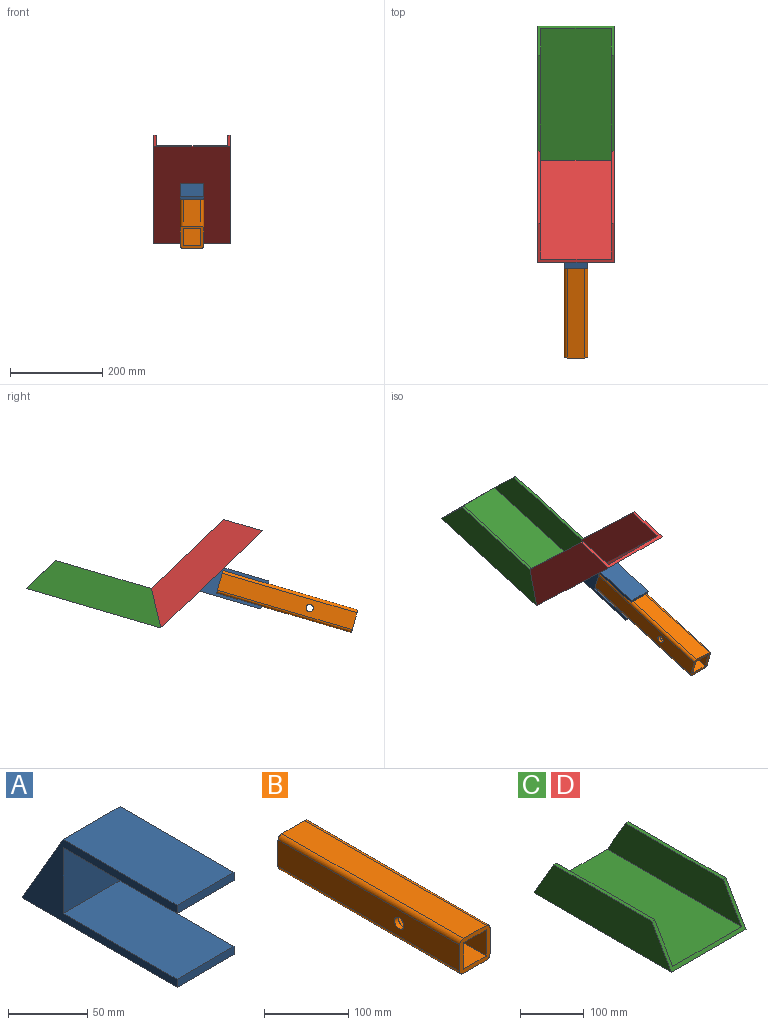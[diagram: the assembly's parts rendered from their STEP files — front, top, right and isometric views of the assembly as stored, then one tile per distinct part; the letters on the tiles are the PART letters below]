
ASSEMBLY  parts=4 mates=3
PART A: 10 faces, bbox 50.8x138.3x63.5 mm
  f0: plane 50.8x50.8mm, normal (0,-1,0), area 2580.6mm2, adj f1,f7,f8,f9
  f1: plane 101.6x50.8mm, normal (0,0,1), area 5161.3mm2, adj f0,f2,f8,f9
  f2: plane 50.8x6.35mm, normal (0,-1,0), area 322.6mm2, adj f1,f3,f8,f9
  f3: plane 138.26x50.8mm, normal (0,0,-1), area 7023.7mm2, adj f2,f4,f8,f9
  f4: plane 63.5x50.8mm, normal (0,0.87,0.5), area 3724.8mm2, adj f3,f5,f8,f9
  f5: plane 101.6x50.8mm, normal (0,0,1), area 5161.3mm2, adj f4,f6,f8,f9
  f6: plane 50.8x6.35mm, normal (0,-1,0), area 322.6mm2, adj f5,f7,f8,f9
  f7: plane 101.6x50.8mm, normal (0,0,-1), area 5161.3mm2, adj f0,f6,f8,f9
  f8: plane 138.26x63.5mm, normal (1,0,0), area 2454.3mm2, adj f0,f1,f2,f3,f4,f5,f6,f7
  f9: plane 138.26x63.5mm, normal (-1,0,0), area 2454.3mm2, adj f0,f1,f2,f3,f4,f5,f6,f7
PART B: 16 faces, bbox 50.8x304.8x50.8 mm
  f0: plane 304.8x38.1mm, normal (1,0,0), area 11414.9mm2, adj f1,f7,f8,f9,f14
  f1: cylinder r=6.35mm len=304.8mm, axis (0,1,0), area 3040.2mm2, adj f0,f2,f8,f9
  f2: plane 304.8x38.1mm, normal (0,0,1), area 11612.9mm2, adj f1,f3,f8,f9
  f3: cylinder r=6.35mm len=304.8mm, axis (0,1,0), area 3040.2mm2, adj f2,f4,f8,f9
  f4: plane 304.8x38.1mm, normal (-1,0,0), area 11414.9mm2, adj f3,f5,f8,f9,f15
  f5: cylinder r=6.35mm len=304.8mm, axis (0,1,0), area 3040.2mm2, adj f4,f6,f8,f9
  f6: plane 304.8x38.1mm, normal (0,0,-1), area 11612.9mm2, adj f5,f7,f8,f9
  f7: cylinder r=6.35mm len=304.8mm, axis (0,1,0), area 3040.2mm2, adj f0,f6,f8,f9
  f8: plane 50.8x50.8mm, normal (0,-1,0), area 1094.4mm2, adj f0,f1,f2,f3,f4,f5,f6,f7
  f9: plane 50.8x50.8mm, normal (0,1,0), area 1094.4mm2, adj f0,f1,f2,f3,f4,f5,f6,f7
  f10: plane 304.8x38.1mm, normal (1,0,0), area 11414.9mm2, adj f8,f9,f11,f13,f15
  f11: plane 304.8x38.1mm, normal (0,0,1), area 11612.9mm2, adj f8,f9,f10,f12
  f12: plane 304.8x38.1mm, normal (-1,0,0), area 11414.9mm2, adj f8,f9,f11,f13,f14
  f13: plane 304.8x38.1mm, normal (0,0,-1), area 11612.9mm2, adj f8,f9,f10,f12
  f14: cylinder r=7.94mm len=15.88mm, axis (1,0,0), area 316.7mm2, adj f0,f12
  f15: cylinder r=7.94mm len=15.88mm, axis (1,0,0), area 316.7mm2, adj f4,f10
PART C: 10 faces, bbox 165.1x304.8x76.2 mm
  f0: plane 216.81x6.35mm, normal (0,0,1), area 1376.8mm2, adj f3,f6,f7,f9
  f1: plane 304.8x76.2mm, normal (-1,0,0), area 19873.4mm2, adj f5,f6,f8,f9
  f2: plane 297.47x152.4mm, normal (0,0,1), area 45334.1mm2, adj f3,f4,f6,f9
  f3: plane 297.47x69.85mm, normal (-1,0,0), area 17961.2mm2, adj f0,f2,f6,f9
  f4: plane 297.47x69.85mm, normal (1,0,0), area 17961.2mm2, adj f2,f6,f8,f9
  f5: plane 304.8x165.1mm, normal (0,0,-1), area 50322.5mm2, adj f1,f6,f7,f9
  f6: plane 165.1x76.2mm, normal (0,0.87,0.5), area 2234.9mm2, adj f0,f1,f2,f3,f4,f5,f7,f8
  f7: plane 304.8x76.2mm, normal (1,0,0), area 19873.4mm2, adj f0,f5,f6,f9
  f8: plane 216.81x6.35mm, normal (0,0,1), area 1376.8mm2, adj f1,f4,f6,f9
  f9: plane 165.1x76.2mm, normal (0,-0.87,0.5), area 2234.9mm2, adj f0,f1,f2,f3,f4,f5,f7,f8
PART D: same geometry as C
PLACE A rot(axis=(1,0,0),16.3deg) t=(-26.03,61.67,-27.65)mm
PLACE B rot(axis=(1,0,0),16.3deg) t=(24.77,59.89,-21.56)mm
PLACE C rot(axis=(0,0.14,-0.99),180deg) t=(75.57,375.57,-40.18)mm
PLACE D rot(axis=(-1,0,0),43.7deg) t=(-76.83,33.6,43.05)mm
MATE fastened A.f0 <-> B.f9  axis (0,-0.96,-0.28) through (-0.63,52.75,2.82)mm
MATE fastened D.f5 <-> A.f4  axis (0,-0.69,-0.72) through (-0.63,70.34,7.97)mm
MATE fastened D.f6 <-> C.f6  axis (0,0.97,-0.24) through (-0.63,186.2,-74.13)mm
